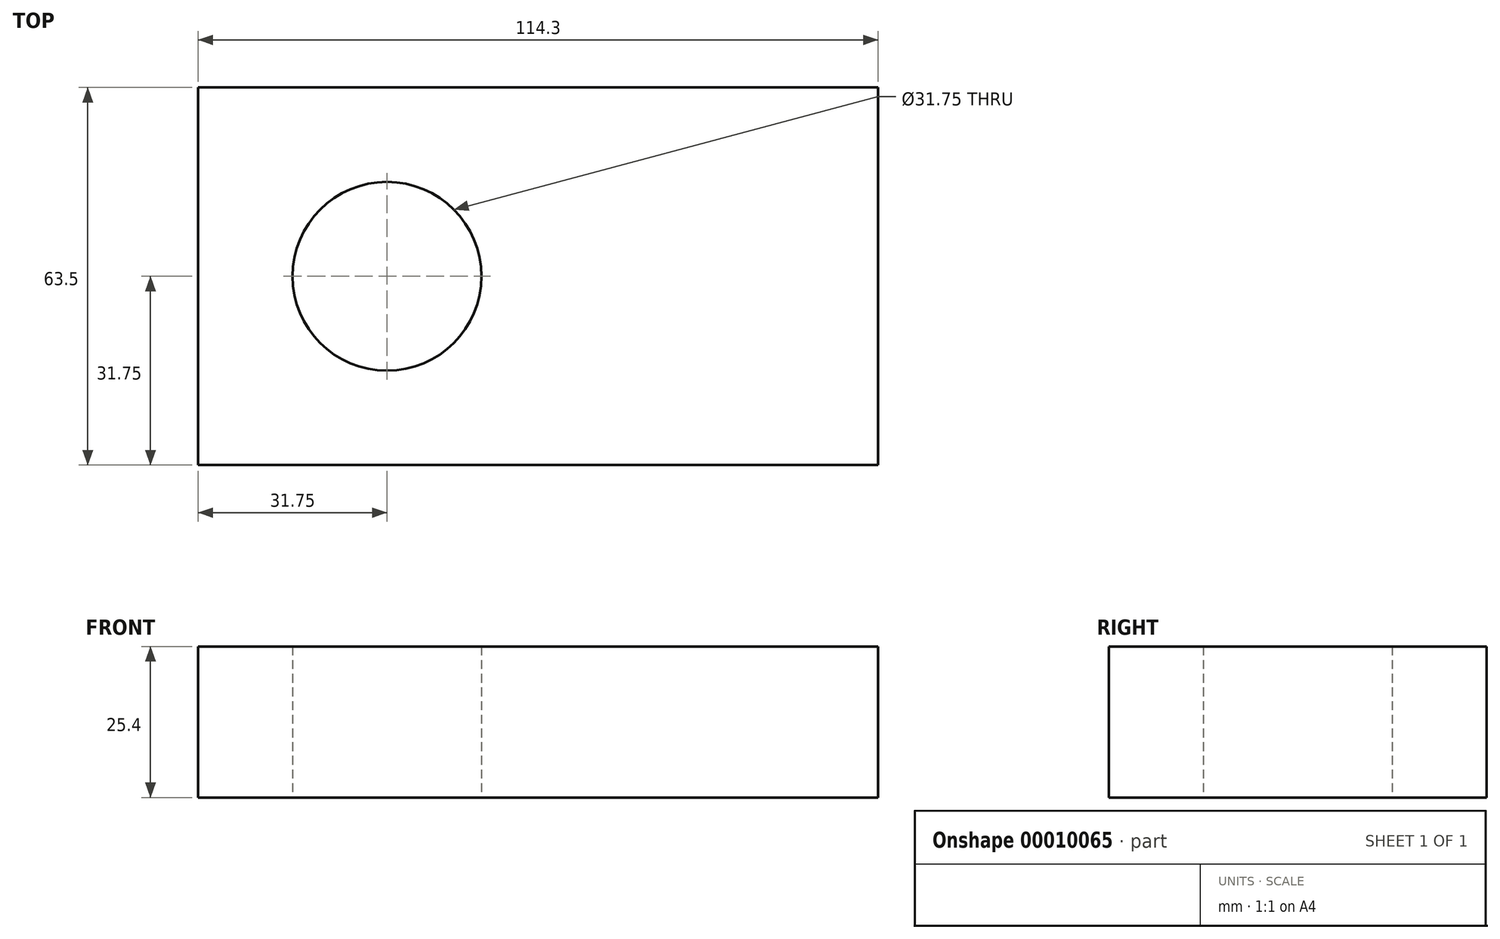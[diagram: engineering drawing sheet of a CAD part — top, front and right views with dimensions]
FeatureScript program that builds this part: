
annotation { "Feature Type Name" : "Feature", "Feature Type Description" : "" }
export const myFeature = defineFeature(function(context is Context, id is Id, definition is map)
    precondition{}
    {
        {
            var Q0;
            Q0=qCreatedBy(makeId("Top.planeOp"),FACE);
            var sketch = newSketch(context, id + "F0", { "sketchPlane" : qUnion([Q0])});
            skLineSegment(sketch, "E0.rect.bottom", {"start": v(-57.15, 31.75) * mm, "end": v(57.15, 31.75) * mm});
            skLineSegment(sketch, "E0.rect.top", {"start": v(-57.15, -31.75) * mm, "end": v(57.15, -31.75) * mm});
            skLineSegment(sketch, "E0.rect.left", {"start": v(-57.15, 31.75) * mm, "end": v(-57.15, -31.75) * mm});
            skLineSegment(sketch, "E0.rect.right", {"start": v(57.15, 31.75) * mm, "end": v(57.15, -31.75) * mm});
            skPoint(sketch, "E0.rect.middle", {"position": v(0, 0) * mm});
            skCircle(sketch, "E1", {"center": v(-25.4, 0) * mm, "radius": 15.88 * mm});
            skSolve(sketch);
        }
        {
            var Q0;
            Q0 = qSketchRegion(id + "F0", true);
            extrude(context, id + "F1", {"entities" : qUnion([Q0]), "depth" : 25.4 * mm});
        }
    });
